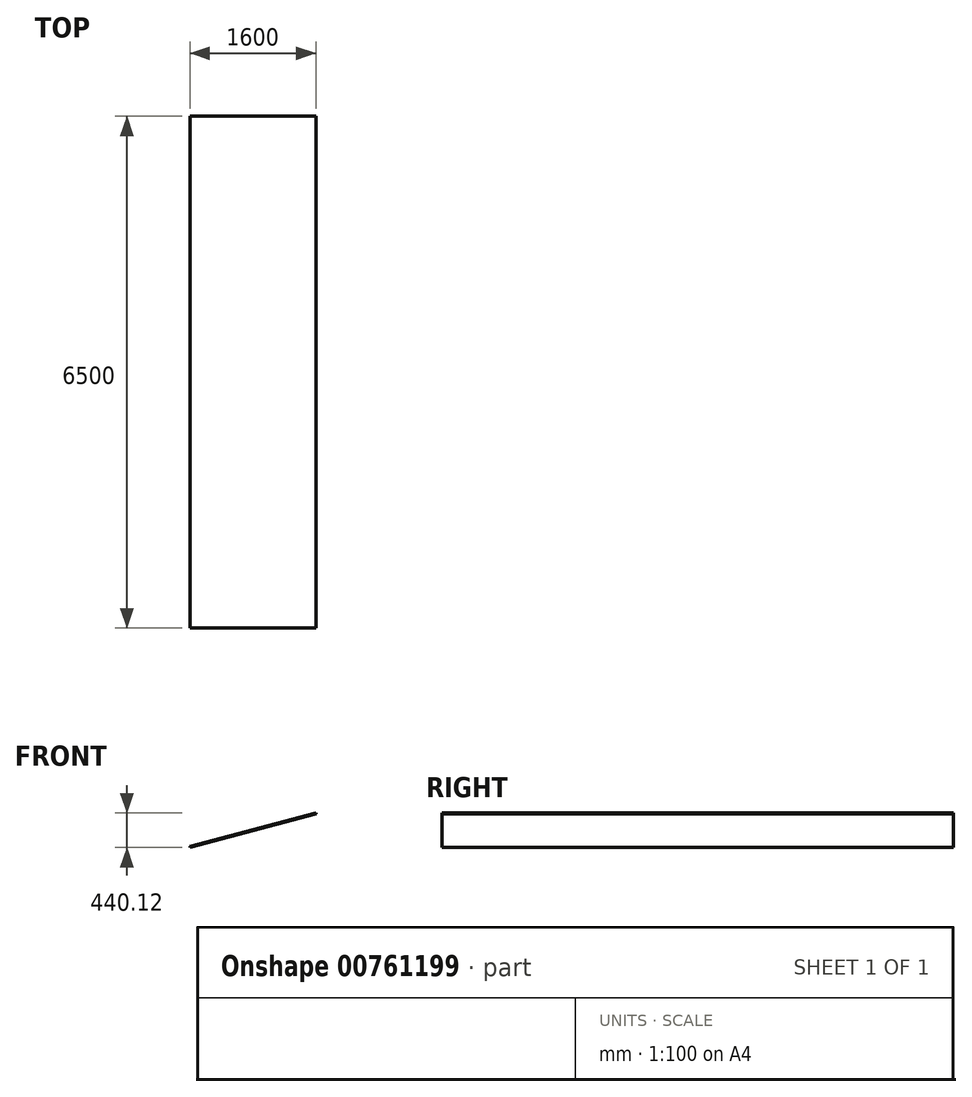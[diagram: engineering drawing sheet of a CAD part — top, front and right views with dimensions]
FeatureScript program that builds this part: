
annotation { "Feature Type Name" : "Feature", "Feature Type Description" : "" }
export const myFeature = defineFeature(function(context is Context, id is Id, definition is map)
    precondition{}
    {
        {
            var Q0;
            Q0=qCreatedBy(makeId("Front.planeOp"),FACE);
            var sketch = newSketch(context, id + "F0", { "sketchPlane" : qUnion([Q0])});
            skLineSegment(sketch, "E0", {"start": v(0, 0) * mm, "end": v(1600, 426.67) * mm});
            skLineSegment(sketch, "E1", {"start": v(0, 13.45) * mm, "end": v(1600, 440.12) * mm});
            skLineSegment(sketch, "E2", {"start": v(0, 13.45) * mm, "end": v(0, 0) * mm});
            skLineSegment(sketch, "E3", {"start": v(1600, 440.12) * mm, "end": v(1600, 426.67) * mm});
            skLineSegment(sketch, "E4", {"start": v(0, 0) * mm, "end": v(1500, 0) * mm, "construction": true});
            skLineSegment(sketch, "E5", {"start": v(1600, 426.67) * mm, "end": v(1600, 0) * mm, "construction": true});
            skSolve(sketch);
        }
        {
            var Q0;
            Q0 = qSketchRegion(id + "F0", true);
            extrude(context, id + "F1", {"entities" : qUnion([Q0]), "depth" : 6500 * mm, "offsetDistance" : 25 * mm});
        }
    });
